# Revit family: QF_Turbo Air_TSR-35_49SD
name_source: partatom
category: Specialty Equipment
revit_build: Autodesk Revit 2014 (Build: 20140709_2115(x64)
units: mm (PartAtom-declared; Revit-internal decimal feet)

## types (2) — shared parameters
Assembly Code = E1090320
CSI MasterFormat = 11 41 13
Cabinet Height = 77"
Conn Plug = NEMA 5-15P
Cycle = 60 Hz
Depth = 30 3/8"
Description = Refrigerator, Reach-In
Door Height = 54 1/2"
Elec Conn Connection Height = 77 7/8"
FL Amps = 9 A
Foodservice Equipment Identifier = Yes
HP = 1/3
Manufacturer = Turbo Air
Phase = 1
Volts = 115 V

## per-type parameters (varying)
| type | Apparent Power | Door Width | Pressure Relief Valve | Weight in Pounds | Width |
| TSR-35SD | 1791 VA | 17 3/4" | Yes | 357 | 39 1/2" |
| TSR-49SD | 1830 VA | 25 1/2" | No | 427 | 54 3/8" |

note: column(s) folded — value = type name in every type: Model

## geometry (parser evidence)
native form markers: Blend x37, Sweep x6
no freeform markers — native parametric forms only
